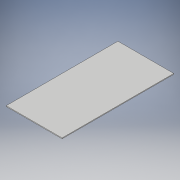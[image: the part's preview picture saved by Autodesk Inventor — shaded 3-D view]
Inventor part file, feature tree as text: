
AUTODESK INVENTOR PART (.ipt)
format: ipt  version: 2017 (Build 210142000, 142)  size: 88,576 bytes
history: native  units: in
note: dims shown in document units (in); Inventor stores cm internally (conversion verified against a paired STEP export)
features: extrude x1, sketch x1
ambient origin geometry x8: Origin, YZ Plane, XZ Plane, XY Plane, X Axis, Y Axis, Z Axis, Center Point
bodies: Solid1 (feature_tree)
feature tree (2):
  extrude  "Extrusion1"  Depth=72.0in
  sketch  "Sketch1"  dims[d0=36.0in d1=72.0in d2=0.5in d3=0.0in]
